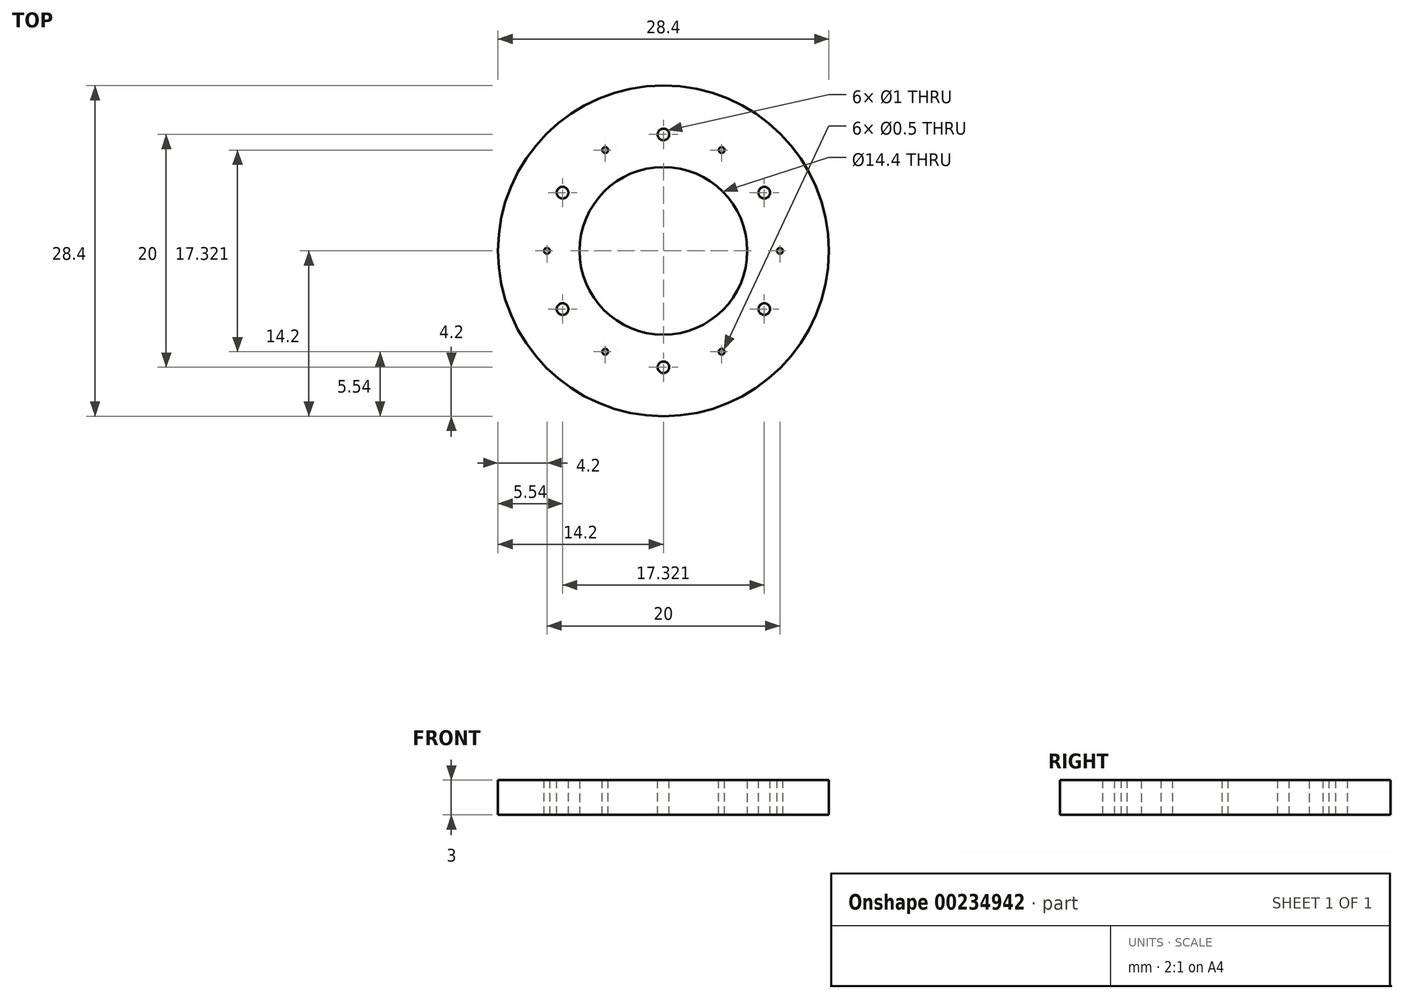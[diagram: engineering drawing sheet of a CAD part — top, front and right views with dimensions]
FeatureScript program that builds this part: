
annotation { "Feature Type Name" : "Feature", "Feature Type Description" : "" }
export const myFeature = defineFeature(function(context is Context, id is Id, definition is map)
    precondition{}
    {
        {
            var Q0;
            Q0=qCreatedBy(makeId("Top.planeOp"),FACE);
            var sketch = newSketch(context, id + "F0", { "sketchPlane" : qUnion([Q0])});
            skCircle(sketch, "E0", {"center": v(0, 0) * mm, "radius": 7.2 * mm});
            skCircle(sketch, "E1", {"center": v(0, 0) * mm, "radius": 14.2 * mm});
            skSolve(sketch);
        }
        {
            var Q0;
            Q0=makeQuery(id+"F0.imprint","IMPRINT",FACE,{"disambiguationData":[TD([[makeQuery(id+"F0.imprint","IMPRINT",EDGE,{"derivedFrom":sQuery(id+"F0.wireOp",EDGE,"E0")}),-1.0]])]});
            extrude(context, id + "F1", {"entities" : qUnion([Q0]), "depth" : 3 * mm});
        }
        {
            var Q0;
            Q0=makeQuery(id+"F1.opExtrude","CAP_FACE",FACE,{"disambiguationData":[OSD([sQuery(id+"F0.wireOp",EDGE,"E0"),sQuery(id+"F0.wireOp",EDGE,"E1")])],"isStart":false});
            var sketch = newSketch(context, id + "F2", { "sketchPlane" : qUnion([Q0])});
            skPoint(sketch, "E2", {"position": v(0, 10) * mm});
            skPoint(sketch, "E3.1.0", {"position": v(-8.66, 5) * mm});
            skPoint(sketch, "E3.2.0", {"position": v(-8.66, -5) * mm});
            skPoint(sketch, "E3.3.0", {"position": v(0, -10) * mm});
            skPoint(sketch, "E3.4.0", {"position": v(8.66, -5) * mm});
            skPoint(sketch, "E3.5.0", {"position": v(8.66, 5) * mm});
            skPoint(sketch, "E3.center", {"position": v(0, 0) * mm});
            skSolve(sketch);
        }
        {
            var Q0;
            Q0=sQuery(id+"F2.wireOp",VERTEX,"E2");
            var Q1;
            Q1=sQuery(id+"F2.wireOp",VERTEX,"E3.5.0");
            var Q2;
            Q2=sQuery(id+"F2.wireOp",VERTEX,"E3.4.0");
            var Q3;
            Q3=sQuery(id+"F2.wireOp",VERTEX,"E3.3.0");
            var Q4;
            Q4=sQuery(id+"F2.wireOp",VERTEX,"E3.1.0");
            var Q5;
            Q5=sQuery(id+"F2.wireOp",VERTEX,"E3.2.0");
            var Q6;
            Q6=makeQuery(id+"F1.opExtrude","SWEPT_BODY",BODY,{"disambiguationData":[OSD([sQuery(id+"F0.wireOp",EDGE,"E0"),sQuery(id+"F0.wireOp",EDGE,"E1")])]});
            hole(context, id + "F3", {"style" : HoleStyle.SIMPLE, "endStyle" : HoleEndStyle.THROUGH, "holeDiameter" : 1 * mm, "locations" : qUnion([Q0, Q1, Q2, Q3, Q4, Q5]), "scope" : qUnion([Q6]), "isTappedThrough" : true});
        }
        {
            var Q0;
            Q0=makeQuery(id+"F1.opExtrude","CAP_FACE",FACE,{"disambiguationData":[OSD([sQuery(id+"F0.wireOp",EDGE,"E0"),sQuery(id+"F0.wireOp",EDGE,"E1")])],"isStart":false});
            var sketch = newSketch(context, id + "F4", { "sketchPlane" : qUnion([Q0])});
            skPoint(sketch, "E4", {"position": v(10, 0) * mm});
            skPoint(sketch, "E5.1.0", {"position": v(5, 8.66) * mm});
            skPoint(sketch, "E5.2.0", {"position": v(-5, 8.66) * mm});
            skPoint(sketch, "E5.3.0", {"position": v(-10, 0) * mm});
            skPoint(sketch, "E5.4.0", {"position": v(-5, -8.66) * mm});
            skPoint(sketch, "E5.5.0", {"position": v(5, -8.66) * mm});
            skPoint(sketch, "E5.center", {"position": v(0, 0) * mm});
            skSolve(sketch);
        }
        {
            var Q0;
            Q0=sQuery(id+"F4.wireOp",VERTEX,"E5.2.0");
            var Q1;
            Q1=sQuery(id+"F4.wireOp",VERTEX,"E5.1.0");
            var Q2;
            Q2=sQuery(id+"F4.wireOp",VERTEX,"E4");
            var Q3;
            Q3=sQuery(id+"F4.wireOp",VERTEX,"E5.5.0");
            var Q4;
            Q4=sQuery(id+"F4.wireOp",VERTEX,"E5.4.0");
            var Q5;
            Q5=sQuery(id+"F4.wireOp",VERTEX,"E5.3.0");
            var Q6;
            Q6=makeQuery(id+"F1.opExtrude","SWEPT_BODY",BODY,{"disambiguationData":[OSD([sQuery(id+"F0.wireOp",EDGE,"E0"),sQuery(id+"F0.wireOp",EDGE,"E1")])]});
            hole(context, id + "F5", {"style" : HoleStyle.SIMPLE, "endStyle" : HoleEndStyle.THROUGH, "holeDiameter" : 0.5 * mm, "locations" : qUnion([Q0, Q1, Q2, Q3, Q4, Q5]), "scope" : qUnion([Q6]), "isTappedThrough" : true});
        }
    });
